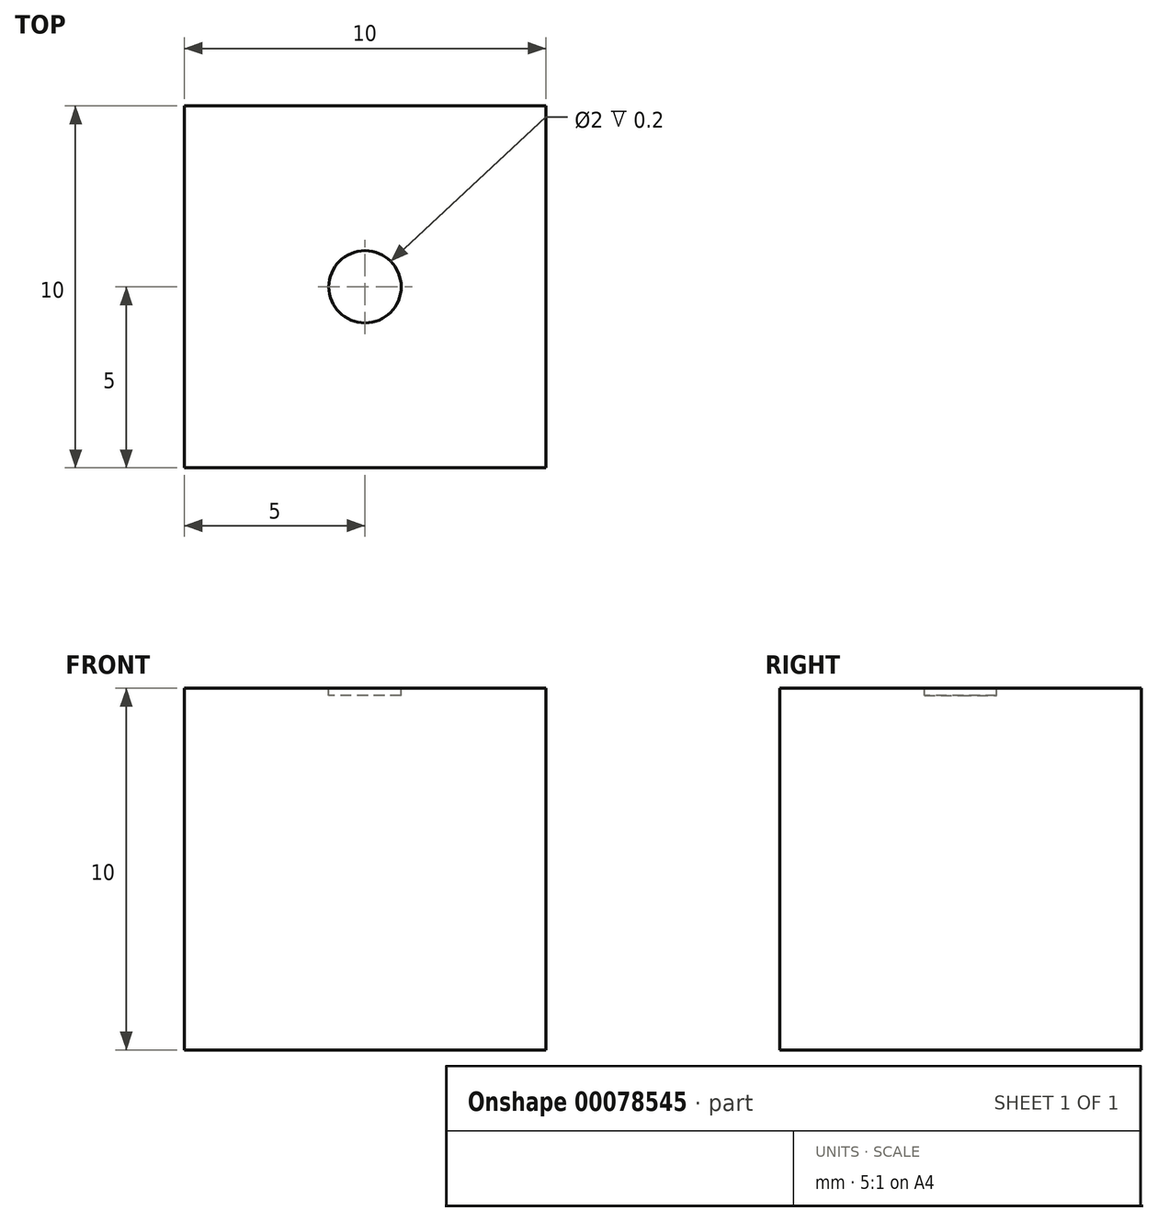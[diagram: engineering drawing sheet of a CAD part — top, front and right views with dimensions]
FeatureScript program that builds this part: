
annotation { "Feature Type Name" : "Feature", "Feature Type Description" : "" }
export const myFeature = defineFeature(function(context is Context, id is Id, definition is map)
    precondition{}
    {
        {
            var Q0;
            Q0=qCreatedBy(makeId("Top.planeOp"),FACE);
            var sketch = newSketch(context, id + "F0", { "sketchPlane" : qUnion([Q0])});
            skLineSegment(sketch, "E0.bottom", {"start": v(0, 0) * mm, "end": v(10, 0) * mm});
            skLineSegment(sketch, "E0.top", {"start": v(0, 10) * mm, "end": v(10, 10) * mm});
            skLineSegment(sketch, "E0.left", {"start": v(0, 0) * mm, "end": v(0, 10) * mm});
            skLineSegment(sketch, "E0.right", {"start": v(10, 0) * mm, "end": v(10, 10) * mm});
            skSolve(sketch);
        }
        {
            var Q0;
            Q0 = qSketchRegion(id + "F0", true);
            extrude(context, id + "F1", {"entities" : qUnion([Q0]), "depth" : 10 * mm});
        }
        {
            var Q0;
            Q0=makeQuery(id+"F1.opExtrude","CAP_FACE",FACE,{"disambiguationData":[OSD([sQuery(id+"F0.wireOp",EDGE,"E0.bottom"),sQuery(id+"F0.wireOp",EDGE,"E0.top"),sQuery(id+"F0.wireOp",EDGE,"E0.left"),sQuery(id+"F0.wireOp",EDGE,"E0.right")])],"isStart":false});
            var sketch = newSketch(context, id + "F2", { "sketchPlane" : qUnion([Q0])});
            skCircle(sketch, "E1", {"center": v(5, 5) * mm, "radius": 1 * mm});
            skSolve(sketch);
        }
        {
            var Q0;
            Q0 = qSketchRegion(id + "F2", true);
            extrude(context, id + "F3", {"entities" : qUnion([Q0]), "operationType" : NewBodyOperationType.REMOVE, "oppositeDirection" : true, "depth" : .2 * mm});
        }
    });
